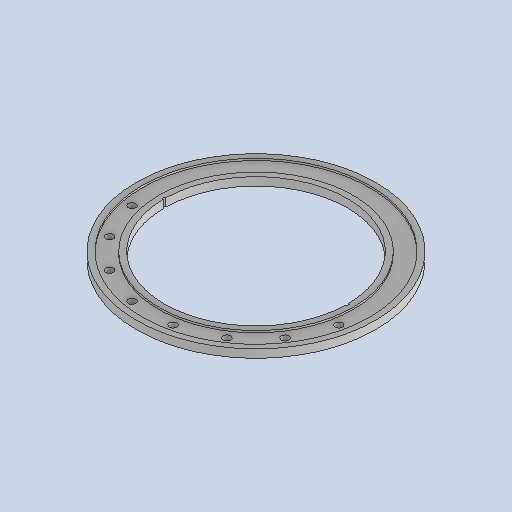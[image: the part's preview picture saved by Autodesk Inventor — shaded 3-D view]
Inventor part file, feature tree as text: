
AUTODESK INVENTOR PART (.ipt)
format: ipt  version: 2025 (Build 290162010, 162A)  size: 231,424 bytes
history: native  units: mm
features: extrude x4, sketch x4, pattern_circular x1, mirror x1, projected_geometry x1, other x1
ambient origin geometry x8: Origin, YZ Plane, XZ Plane, XY Plane, X Axis, Y Axis, Z Axis, Center Point
bodies: Solid1 (feature_tree)
feature tree (12):
  extrude  "Extrusion1"  Depth=15.0mm
  extrude  "Extrusion2"  TaperAngle=0.0deg  [1 undecoded]
  extrude  "Extrusion3"  Depth=52.0mm
  pattern_circular  "Circular Pattern2"  Count=39  [1 undecoded]
  extrude  "Extrusion4"  Depth=14.0mm
  mirror  "Mirror1"
  sketch  "Sketch1"  dims[d2=15.0mm d3=0.0mm d4=31.0mm]
  sketch  "Sketch2"  dims[d6=3.5mm d7=0.0mm d10=0.0mm d11=0.0mm]
  projected_geometry  "Projected Loop1"
  sketch  "Sketch3"  dims[d17=390.0mm d18=52.0mm d19=390.0mm]
  sketch  "Sketch5"  dims[d20=1.963495mm d21=14.0mm d22=80.0mm d23=157.5deg d34=0.0mm d35=0.0mm d36=5.0mm]
  other  "Definition1"
note: 2 required parameter values undecoded (feature->parameter linkage not recoverable at this tier; creation-order binding heuristic only, values carry confidence <= 0.55)
